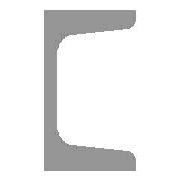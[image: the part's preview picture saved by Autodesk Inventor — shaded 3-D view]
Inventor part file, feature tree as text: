
AUTODESK INVENTOR PART (.ipt)
format: ipt  version: 2025 (Build 290162010, 162A)  size: 138,752 bytes
history: native  units: mm (DEFAULTED — no unit token found)
features: other x3, sketch x1, plane x1
ambient origin geometry x8: Origin, YZ Plane, XZ Plane, XY Plane, X Axis, Y Axis, Z Axis, Center Point
bodies: Solid1 (feature_tree), Body (feature_tree)
feature tree (5):
  other  "Driven Length"
  other  "Start plane"
  other  "End plane"
  sketch  "Sketch3"  dims[d0=5.9mm d1=50.0mm d2=50.0mm d3=8.0mm d4=22.05mm d5=2.317543mm d6=2200.0mm d7=0.0mm d23=8.0mm d24=4.5mm d25=1.51mm d26=-0.0mm d27=2200.0mm d28=90.0deg d29=2200.0mm]
  plane  "Work Plane3"
